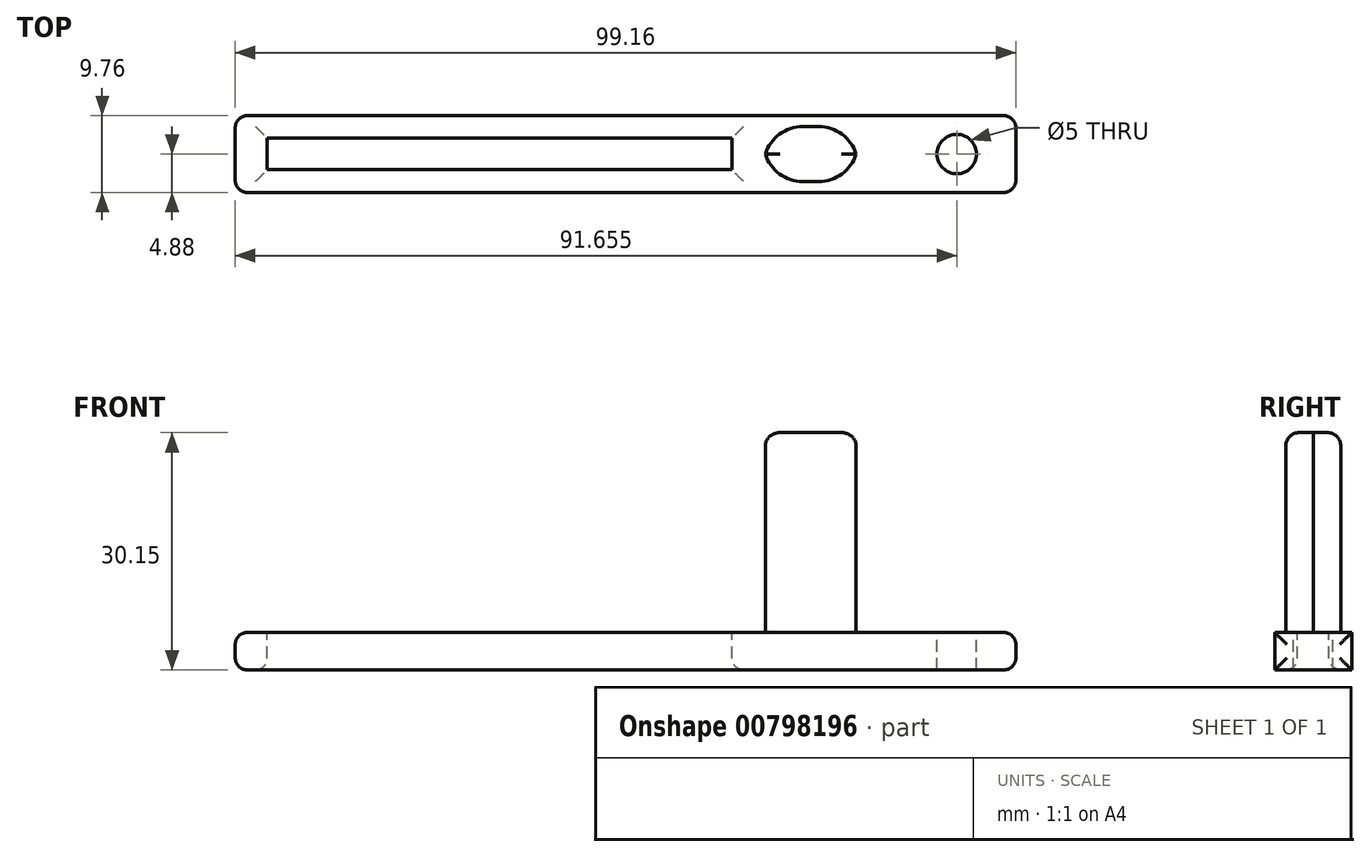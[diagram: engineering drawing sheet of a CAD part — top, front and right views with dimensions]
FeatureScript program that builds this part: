
annotation { "Feature Type Name" : "Feature", "Feature Type Description" : "" }
export const myFeature = defineFeature(function(context is Context, id is Id, definition is map)
    precondition{}
    {
        {
            var Q0;
            Q0=qCreatedBy(makeId("Top.planeOp"),FACE);
            var sketch = newSketch(context, id + "F0", { "sketchPlane" : qUnion([Q0])});
            skLineSegment(sketch, "E0.bottom", {"start": v(-49.58, 4.88) * mm, "end": v(49.58, 4.88) * mm});
            skLineSegment(sketch, "E0.top", {"start": v(-49.58, -4.88) * mm, "end": v(49.58, -4.88) * mm});
            skLineSegment(sketch, "E0.left", {"start": v(-49.58, 4.88) * mm, "end": v(-49.58, -4.88) * mm});
            skLineSegment(sketch, "E0.right", {"start": v(49.58, 4.88) * mm, "end": v(49.58, -4.88) * mm});
            skPoint(sketch, "E0.middle", {"position": v(0, 0) * mm});
            skSolve(sketch);
        }
        {
            var Q0;
            Q0 = qSketchRegion(id + "F0", true);
            extrude(context, id + "F1", {"entities" : qUnion([Q0]), "depth" : 4.75 * mm, "offsetDistance" : 25 * mm});
        }
        {
            var Q0;
            Q0=makeQuery(id+"F1.opExtrude","CAP_FACE",FACE,{"disambiguationData":[OSD([sQuery(id+"F0.wireOp",EDGE,"E0.bottom"),sQuery(id+"F0.wireOp",EDGE,"E0.top"),sQuery(id+"F0.wireOp",EDGE,"E0.left"),sQuery(id+"F0.wireOp",EDGE,"E0.right")])],"isStart":false});
            var sketch = newSketch(context, id + "F2", { "sketchPlane" : qUnion([Q0])});
            skCircle(sketch, "E1", {"center": v(42.08, 0) * mm, "radius": 2.5 * mm});
            skSolve(sketch);
        }
        {
            var Q0;
            Q0=makeQuery(id+"F2.imprint","IMPRINT",FACE,{"disambiguationData":[TD([[makeQuery(id+"F2.imprint","IMPRINT",EDGE,{"derivedFrom":sQuery(id+"F2.wireOp",EDGE,"E1")}),1.0]])]});
            extrude(context, id + "F3", {"entities" : qUnion([Q0]), "operationType" : NewBodyOperationType.REMOVE, "endBound" : BoundingType.THROUGH_ALL, "oppositeDirection" : true, "depth" : 25 * mm, "offsetDistance" : 25 * mm});
        }
        {
            var Q0;
            Q0=makeQuery(id+"F1.opExtrude","CAP_FACE",FACE,{"disambiguationData":[OSD([sQuery(id+"F0.wireOp",EDGE,"E0.bottom"),sQuery(id+"F0.wireOp",EDGE,"E0.top"),sQuery(id+"F0.wireOp",EDGE,"E0.left"),sQuery(id+"F0.wireOp",EDGE,"E0.right")])],"isStart":false});
            var sketch = newSketch(context, id + "F4", { "sketchPlane" : qUnion([Q0])});
            skLineSegment(sketch, "E2.bottom", {"start": v(29.52, 3.5) * mm, "end": v(17.52, 3.5) * mm});
            skLineSegment(sketch, "E2.top", {"start": v(29.52, -3.5) * mm, "end": v(17.52, -3.5) * mm});
            skLineSegment(sketch, "E2.left", {"start": v(29.52, 3.5) * mm, "end": v(29.52, -3.5) * mm});
            skLineSegment(sketch, "E2.right", {"start": v(17.52, 3.5) * mm, "end": v(17.52, -3.5) * mm});
            skSolve(sketch);
        }
        {
            var Q0;
            Q0=makeQuery(id+"F4.imprint","IMPRINT",FACE,{"disambiguationData":[TD([[makeQuery(id+"F4.imprint","IMPRINT",EDGE,{"derivedFrom":sQuery(id+"F4.wireOp",EDGE,"E2.bottom")}),1.0]])]});
            extrude(context, id + "F5", {"entities" : qUnion([Q0]), "operationType" : NewBodyOperationType.ADD, "depth" : 25.4 * mm, "offsetDistance" : 25 * mm});
        }
        {
            var Q0;
            Q0=makeQuery(id+"F5.opExtrude","SWEPT_EDGE",EDGE,{"disambiguationData":[OSD([sQuery(id+"F4.wireOp",EDGE,"E2.bottom"),sQuery(id+"F4.wireOp",EDGE,"E2.right")])]});
            var Q1;
            Q1=makeQuery(id+"F5.opExtrude","SWEPT_EDGE",EDGE,{"disambiguationData":[OSD([sQuery(id+"F4.wireOp",EDGE,"E2.top"),sQuery(id+"F4.wireOp",EDGE,"E2.right")])]});
            var Q2;
            Q2=makeQuery(id+"F5.opExtrude","SWEPT_EDGE",EDGE,{"disambiguationData":[OSD([sQuery(id+"F4.wireOp",EDGE,"E2.bottom"),sQuery(id+"F4.wireOp",EDGE,"E2.left")])]});
            var Q3;
            Q3=makeQuery(id+"F5.opExtrude","SWEPT_EDGE",EDGE,{"disambiguationData":[OSD([sQuery(id+"F4.wireOp",EDGE,"E2.top"),sQuery(id+"F4.wireOp",EDGE,"E2.left")])]});
            fillet(context, id + "F6", {"entities" : qUnion([Q0, Q1, Q2, Q3]), "radius" : 5 * mm, "tangentPropagation" : true, "allowEdgeOverflow" : false});
        }
        {
            var Q0;
            Q0=makeQuery(id+"F1.opExtrude","SWEPT_FACE",FACE,{"disambiguationData":[OSD([sQuery(id+"F0.wireOp",EDGE,"E0.left")])]});
            var Q1;
            Q1=makeQuery(id+"F1.opExtrude","SWEPT_FACE",FACE,{"disambiguationData":[OSD([sQuery(id+"F0.wireOp",EDGE,"E0.right")])]});
            fillet(context, id + "F7", {"entities" : qUnion([Q0, Q1]), "radius" : 1.5 * mm, "tangentPropagation" : true, "allowEdgeOverflow" : false});
        }
        {
            var Q0;
            Q0=makeQuery(id+"F5.opExtrude","CAP_FACE",FACE,{"disambiguationData":[OSD([sQuery(id+"F4.wireOp",EDGE,"E2.bottom"),sQuery(id+"F4.wireOp",EDGE,"E2.top"),sQuery(id+"F4.wireOp",EDGE,"E2.left"),sQuery(id+"F4.wireOp",EDGE,"E2.right")])],"isStart":false});
            fillet(context, id + "F8", {"entities" : qUnion([Q0]), "radius" : 1.75 * mm, "tangentPropagation" : true, "allowEdgeOverflow" : false});
        }
        {
            var Q0;
            Q0=makeQuery(id+"F2.imprint","IMPRINT",FACE,{"disambiguationData":[TD([[makeQuery(id+"F2.imprint","IMPRINT",EDGE,{"derivedFrom":sQuery(id+"F2.wireOp",EDGE,"E1")}),-1.0]])]});
            var sketch = newSketch(context, id + "F9", { "sketchPlane" : qUnion([Q0])});
            skLineSegment(sketch, "E3.bottom", {"start": v(-45.5, 2) * mm, "end": v(13.5, 2) * mm});
            skLineSegment(sketch, "E3.top", {"start": v(-45.5, -2) * mm, "end": v(13.5, -2) * mm});
            skLineSegment(sketch, "E3.left", {"start": v(-45.5, 2) * mm, "end": v(-45.5, -2) * mm});
            skLineSegment(sketch, "E3.right", {"start": v(13.5, 2) * mm, "end": v(13.5, -2) * mm});
            skSolve(sketch);
        }
        {
            var Q0;
            Q0 = qSketchRegion(id + "F9", true);
            extrude(context, id + "F10", {"entities" : qUnion([Q0]), "operationType" : NewBodyOperationType.REMOVE, "oppositeDirection" : true, "depth" : 25 * mm, "offsetDistance" : 25 * mm});
        }
        {
            var Q0;
            Q0=makeQuery(id+"F10.boolean.opBoolean","COPY",EDGE,{"derivedFrom":makeQuery(id+"F10.opExtrude","CAP_EDGE",EDGE,{"disambiguationData":[OSD([sQuery(id+"F9.wireOp",EDGE,"E3.bottom")])],"isStart":true})});
            var Q1;
            Q1=makeQuery(id+"F10.boolean.opBoolean","COPY",EDGE,{"derivedFrom":makeQuery(id+"F10.opExtrude","CAP_EDGE",EDGE,{"disambiguationData":[OSD([sQuery(id+"F9.wireOp",EDGE,"E3.left")])],"isStart":true})});
            var Q2;
            Q2=makeQuery(id+"F10.boolean.opBoolean","COPY",EDGE,{"derivedFrom":makeQuery(id+"F10.opExtrude","CAP_EDGE",EDGE,{"disambiguationData":[OSD([sQuery(id+"F9.wireOp",EDGE,"E3.top")])],"isStart":true})});
            var Q3;
            Q3=makeQuery(id+"F10.boolean.opBoolean","COPY",EDGE,{"derivedFrom":makeQuery(id+"F10.opExtrude","CAP_EDGE",EDGE,{"disambiguationData":[OSD([sQuery(id+"F9.wireOp",EDGE,"E3.right")])],"isStart":true})});
            var Q4;
            Q4=makeQuery(id+"F10.boolean.opBoolean","INTERSECT",EDGE,{"derivedFrom":[makeQuery(id+"F1.opExtrude","CAP_FACE",FACE,{"disambiguationData":[OSD([sQuery(id+"F0.wireOp",EDGE,"E0.bottom"),sQuery(id+"F0.wireOp",EDGE,"E0.top"),sQuery(id+"F0.wireOp",EDGE,"E0.left"),sQuery(id+"F0.wireOp",EDGE,"E0.right")])],"isStart":true}),makeQuery(id+"F10.opExtrude","SWEPT_FACE",FACE,{"disambiguationData":[OSD([sQuery(id+"F9.wireOp",EDGE,"E3.right")])]})]});
            var Q5;
            Q5=makeQuery(id+"F10.boolean.opBoolean","INTERSECT",EDGE,{"derivedFrom":[makeQuery(id+"F1.opExtrude","CAP_FACE",FACE,{"disambiguationData":[OSD([sQuery(id+"F0.wireOp",EDGE,"E0.bottom"),sQuery(id+"F0.wireOp",EDGE,"E0.top"),sQuery(id+"F0.wireOp",EDGE,"E0.left"),sQuery(id+"F0.wireOp",EDGE,"E0.right")])],"isStart":true}),makeQuery(id+"F10.opExtrude","SWEPT_FACE",FACE,{"disambiguationData":[OSD([sQuery(id+"F9.wireOp",EDGE,"E3.bottom")])]})]});
            var Q6;
            Q6=makeQuery(id+"F10.boolean.opBoolean","INTERSECT",EDGE,{"derivedFrom":[makeQuery(id+"F1.opExtrude","CAP_FACE",FACE,{"disambiguationData":[OSD([sQuery(id+"F0.wireOp",EDGE,"E0.bottom"),sQuery(id+"F0.wireOp",EDGE,"E0.top"),sQuery(id+"F0.wireOp",EDGE,"E0.left"),sQuery(id+"F0.wireOp",EDGE,"E0.right")])],"isStart":true}),makeQuery(id+"F10.opExtrude","SWEPT_FACE",FACE,{"disambiguationData":[OSD([sQuery(id+"F9.wireOp",EDGE,"E3.top")])]})]});
            var Q7;
            Q7=makeQuery(id+"F10.boolean.opBoolean","INTERSECT",EDGE,{"derivedFrom":[makeQuery(id+"F1.opExtrude","CAP_FACE",FACE,{"disambiguationData":[OSD([sQuery(id+"F0.wireOp",EDGE,"E0.bottom"),sQuery(id+"F0.wireOp",EDGE,"E0.top"),sQuery(id+"F0.wireOp",EDGE,"E0.left"),sQuery(id+"F0.wireOp",EDGE,"E0.right")])],"isStart":true}),makeQuery(id+"F10.opExtrude","SWEPT_FACE",FACE,{"disambiguationData":[OSD([sQuery(id+"F9.wireOp",EDGE,"E3.left")])]})]});
            fillet(context, id + "F11", {"entities" : qUnion([Q0, Q1, Q2, Q3, Q4, Q5, Q6, Q7]), "radius" : 1.5 * mm, "tangentPropagation" : true, "allowEdgeOverflow" : false});
        }
    });
